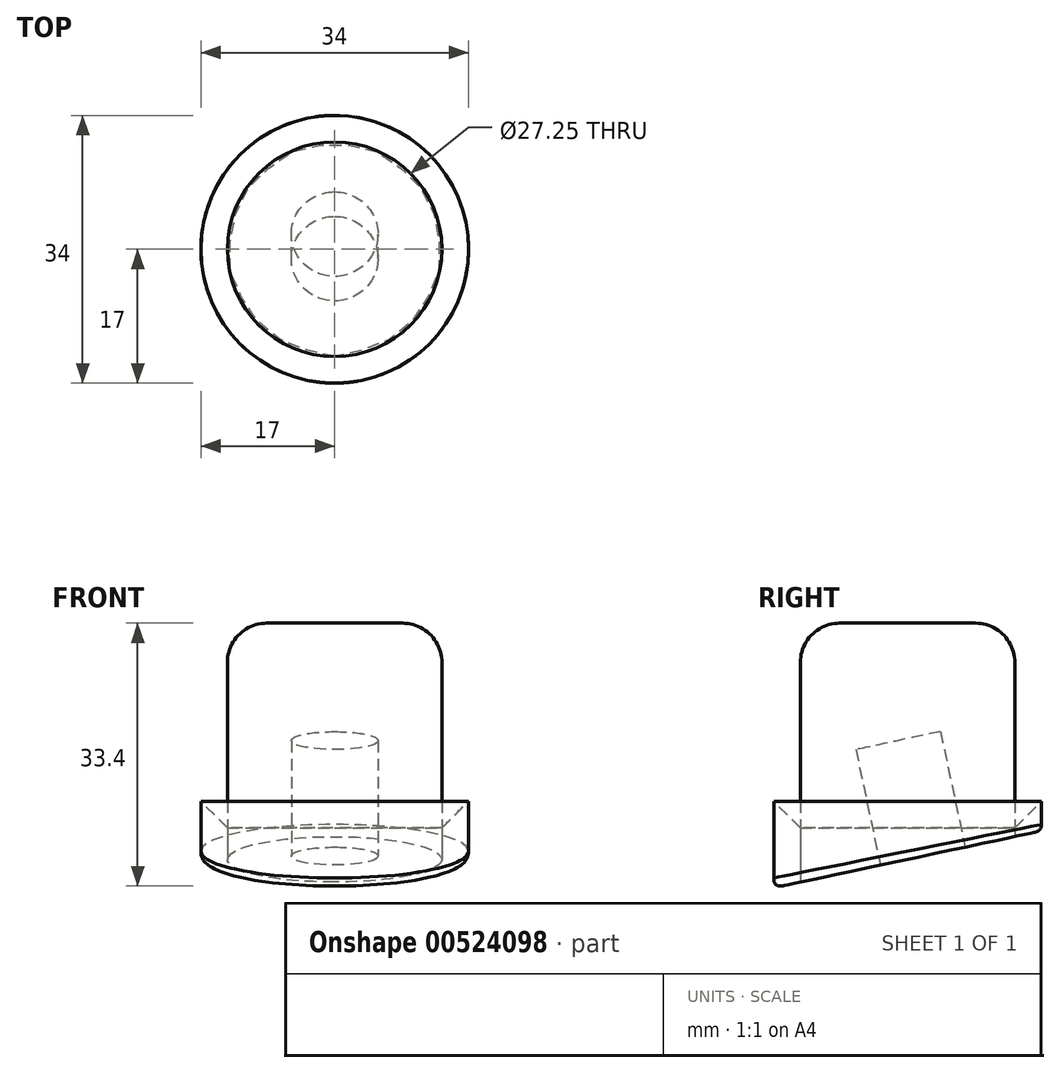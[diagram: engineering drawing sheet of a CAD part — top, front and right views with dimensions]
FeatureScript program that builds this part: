
annotation { "Feature Type Name" : "Feature", "Feature Type Description" : "" }
export const myFeature = defineFeature(function(context is Context, id is Id, definition is map)
    precondition{}
    {
        {
            var Q0;
            Q0=qCreatedBy(makeId("Top.planeOp"),FACE);
            var sketch = newSketch(context, id + "F0", { "sketchPlane" : qUnion([Q0])});
            skLineSegment(sketch, "E0", {"start": v(-30.36, 0) * mm, "end": v(39.37, 0) * mm});
            skSolve(sketch);
        }
        {
            var Q0;
            Q0=qCreatedBy(makeId("Top.planeOp"),FACE);
            var Q1;
            Q1=sQuery(id+"F0.wireOp",EDGE,"E0");
            cPlane(context, id + "F1", {"entities" : qUnion([Q0, Q1]), "cplaneType" : CPlaneType.LINE_ANGLE, "offset" : 25 * mm, "angle" : 12 * degree, "width" : 150 * mm, "height" : 150 * mm});
        }
        {
            var Q0;
            Q0=qCreatedBy(makeId("Top.planeOp"),FACE);
            var sketch = newSketch(context, id + "F2", { "sketchPlane" : qUnion([Q0])});
            skCircle(sketch, "E1", {"center": v(0, 0) * mm, "radius": 13.63 * mm});
            skSolve(sketch);
        }
        {
            var Q0;
            Q0=qSketchRegion(id+"F2",true);
            var Q1;
            Q1=qBodyType(qCreatedBy(id+"F1",FACE),BodyType.SOLID);
            extrude(context, id + "F3", {"entities" : qUnion([Q0]), "endBound" : BoundingType.SYMMETRIC, "depth" : 60 * mm, "endBoundEntityFace" : qUnion([Q1]), "offsetDistance" : 25 * mm});
        }
        {
            var Q0;
            Q0=makeQuery(id+"F3.opExtrude","CAP_EDGE",EDGE,{"disambiguationData":[OSD([sQuery(id+"F2.wireOp",EDGE,"E1")])],"isStart":false});
            fillet(context, id + "F4", {"entities" : qUnion([Q0]), "radius" : 5 * mm, "tangentPropagation" : true, "allowEdgeOverflow" : false});
        }
        {
            var Q0;
            Q0=qCreatedBy(id+"F1.planeOp",FACE);
            var sketch = newSketch(context, id + "F5", { "sketchPlane" : qUnion([Q0])});
            skCircle(sketch, "E2", {"center": v(0, -1.96) * mm, "radius": 5.5 * mm});
            skSolve(sketch);
        }
        {
            var Q0;
            Q0=qSketchRegion(id+"F5",true);
            extrude(context, id + "F6", {"entities" : qUnion([Q0]), "endBound" : BoundingType.SYMMETRIC, "oppositeDirection" : true, "depth" : 30 * mm, "offsetDistance" : 25 * mm});
        }
        {
            var Q0;
            Q0=qCreatedBy(makeId("Top.planeOp"),FACE);
            var sketch = newSketch(context, id + "F7", { "sketchPlane" : qUnion([Q0])});
            skCircle(sketch, "E3", {"center": v(0, 0) * mm, "radius": 13.62 * mm});
            skCircle(sketch, "E4", {"center": v(0, 0) * mm, "radius": 17 * mm});
            skLineSegment(sketch, "E5", {"start": v(-28.46, 0) * mm, "end": v(40.56, 0) * mm});
            skSolve(sketch);
        }
        {
            var Q0;
            Q0=qSketchRegion(id+"F7",true);
            extrude(context, id + "F8", {"entities" : qUnion([Q0]), "endBound" : BoundingType.SYMMETRIC, "depth" : 16 * mm, "offsetDistance" : 25 * mm});
        }
        {
            var Q0;
            Q0=makeQuery(id+"F8.opExtrude","CAP_EDGE",EDGE,{"disambiguationData":[OSD([sQuery(id+"F7.wireOp",EDGE,"E3")])],"isStart":false});
            chamfer(context, id + "F9", {"entities" : qUnion([Q0]), "width" : 4 * mm, "tangentPropagation" : true});
        }
        {
            var Q0;
            Q0=makeQuery(id+"F6.opExtrude","SWEPT_BODY",BODY,{"disambiguationData":[OSD([sQuery(id+"F5.wireOp",EDGE,"E2")])]});
            var Q1;
            Q1=makeQuery(id+"F3.opExtrude","SWEPT_BODY",BODY,{"disambiguationData":[OSD([sQuery(id+"F2.wireOp",EDGE,"E1")])]});
            booleanBodies(context, id + "F10", {"operationType" : BooleanOperationType.SUBTRACTION, "tools" : qUnion([Q0]), "targets" : qUnion([Q1])});
        }
        {
            var Q0;
            Q0=qCreatedBy(id+"F1.planeOp",FACE);
            var sketch = newSketch(context, id + "F11", { "sketchPlane" : qUnion([Q0])});
            skCircle(sketch, "E6", {"center": v(0, 0) * mm, "radius": 25 * mm});
            skSolve(sketch);
        }
        {
            var Q0;
            Q0=qSketchRegion(id+"F11",true);
            extrude(context, id + "F12", {"entities" : qUnion([Q0]), "depth" : 55 * mm, "offsetDistance" : 25 * mm});
        }
        {
            var Q0;
            Q0=makeQuery(id+"F12.opExtrude","SWEPT_BODY",BODY,{"disambiguationData":[OSD([sQuery(id+"F11.wireOp",EDGE,"E6")])]});
            var Q1;
            Q1=makeQuery(id+"F3.opExtrude","SWEPT_BODY",BODY,{"disambiguationData":[OSD([sQuery(id+"F2.wireOp",EDGE,"E1")])]});
            var Q2;
            Q2=makeQuery(id+"F8.opExtrude","SWEPT_BODY",BODY,{"disambiguationData":[OSD([sQuery(id+"F7.wireOp",EDGE,"E3"),sQuery(id+"F7.wireOp",EDGE,"E4")])]});
            booleanBodies(context, id + "F13", {"operationType" : BooleanOperationType.SUBTRACTION, "tools" : qUnion([Q0]), "targets" : qUnion([Q1, Q2])});
        }
        {
            var Q0;
            Q0=makeQuery(id+"F13.opBoolean","INTERSECT",EDGE,{"derivedFrom":[makeQuery(id+"F8.opExtrude","SWEPT_FACE",FACE,{"disambiguationData":[OSD([sQuery(id+"F7.wireOp",EDGE,"E4")])]}),makeQuery(id+"F12.opExtrude","CAP_FACE",FACE,{"disambiguationData":[OSD([sQuery(id+"F11.wireOp",EDGE,"E6")])],"isStart":true})]});
            fillet(context, id + "F14", {"entities" : qUnion([Q0]), "radius" : 1 * mm, "rho" : 0.5, "crossSection" : FilletCrossSection.CONIC, "allowEdgeOverflow" : false});
        }
    });
